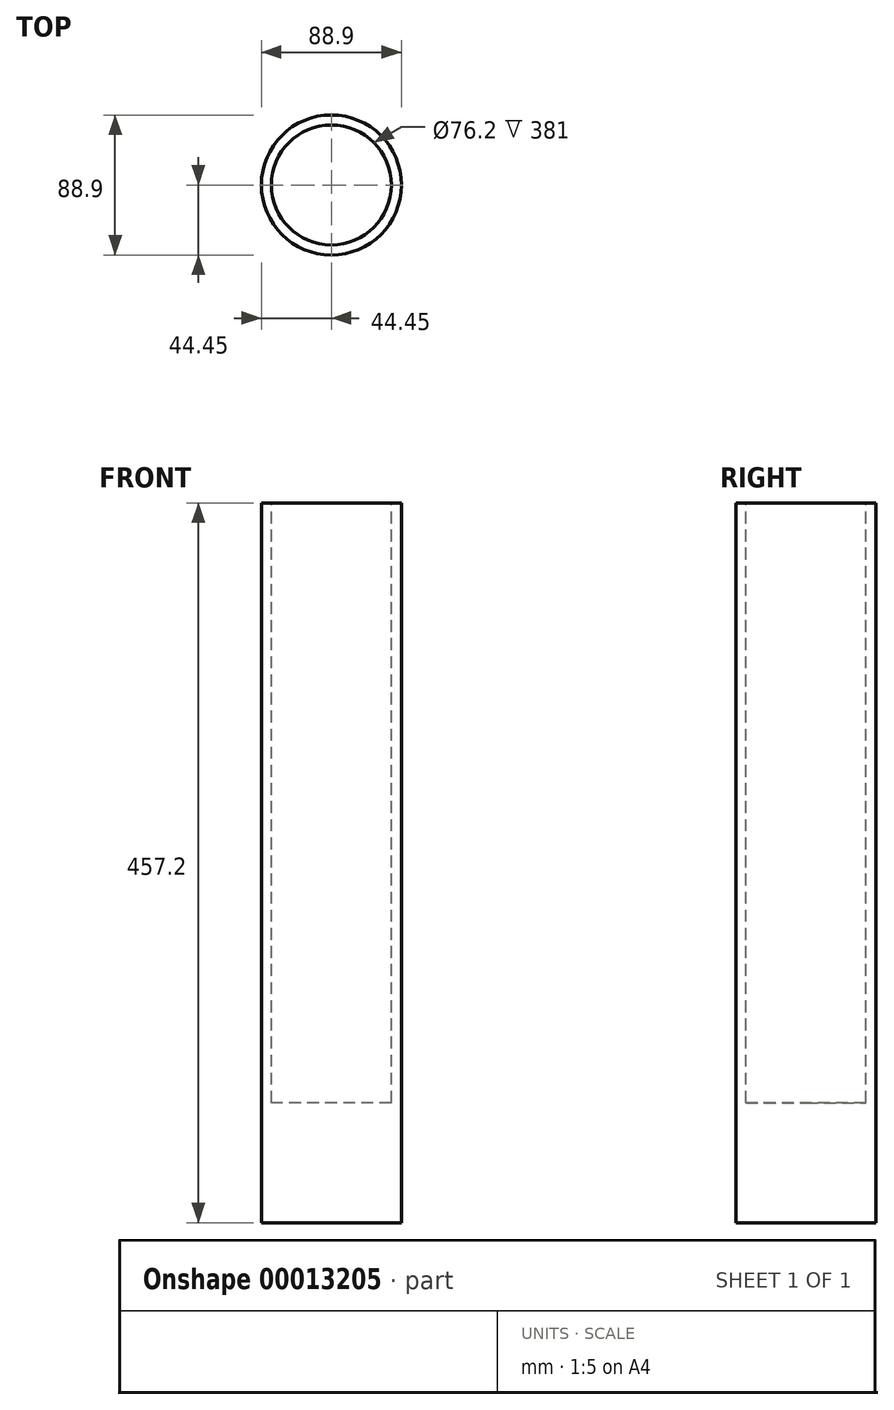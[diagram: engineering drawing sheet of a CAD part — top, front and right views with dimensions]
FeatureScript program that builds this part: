
annotation { "Feature Type Name" : "Feature", "Feature Type Description" : "" }
export const myFeature = defineFeature(function(context is Context, id is Id, definition is map)
    precondition{}
    {
        {
            var Q0;
            Q0=qCreatedBy(makeId("Top.planeOp"),FACE);
            var sketch = newSketch(context, id + "F0", { "sketchPlane" : qUnion([Q0])});
            skCircle(sketch, "E0", {"center": v(0, 0) * mm, "radius": 44.45 * mm});
            skSolve(sketch);
        }
        {
            var Q0;
            Q0=makeQuery(id+"F0.imprint","IMPRINT",FACE,{"disambiguationData":[TD([[makeQuery(id+"F0.imprint","IMPRINT",EDGE,{"derivedFrom":sQuery(id+"F0.wireOp",EDGE,"E0")}),1.0]])]});
            extrude(context, id + "F1", {"entities" : qUnion([Q0]), "depth" : 457.2 * mm, "offsetDistance" : 25.4 * mm});
        }
        {
            var Q0;
            Q0=makeQuery(id+"F1.opExtrude","CAP_FACE",FACE,{"disambiguationData":[OSD([sQuery(id+"F0.wireOp",EDGE,"E0")])],"isStart":false});
            var sketch = newSketch(context, id + "F2", { "sketchPlane" : qUnion([Q0])});
            skCircle(sketch, "E1", {"center": v(0, 0) * mm, "radius": 38.1 * mm});
            skSolve(sketch);
        }
        {
            var Q0;
            Q0 = qSketchRegion(id + "F2", true);
            extrude(context, id + "F3", {"entities" : qUnion([Q0]), "operationType" : NewBodyOperationType.REMOVE, "depth" : -381 * mm, "offsetDistance" : 25.4 * mm});
        }
    });
